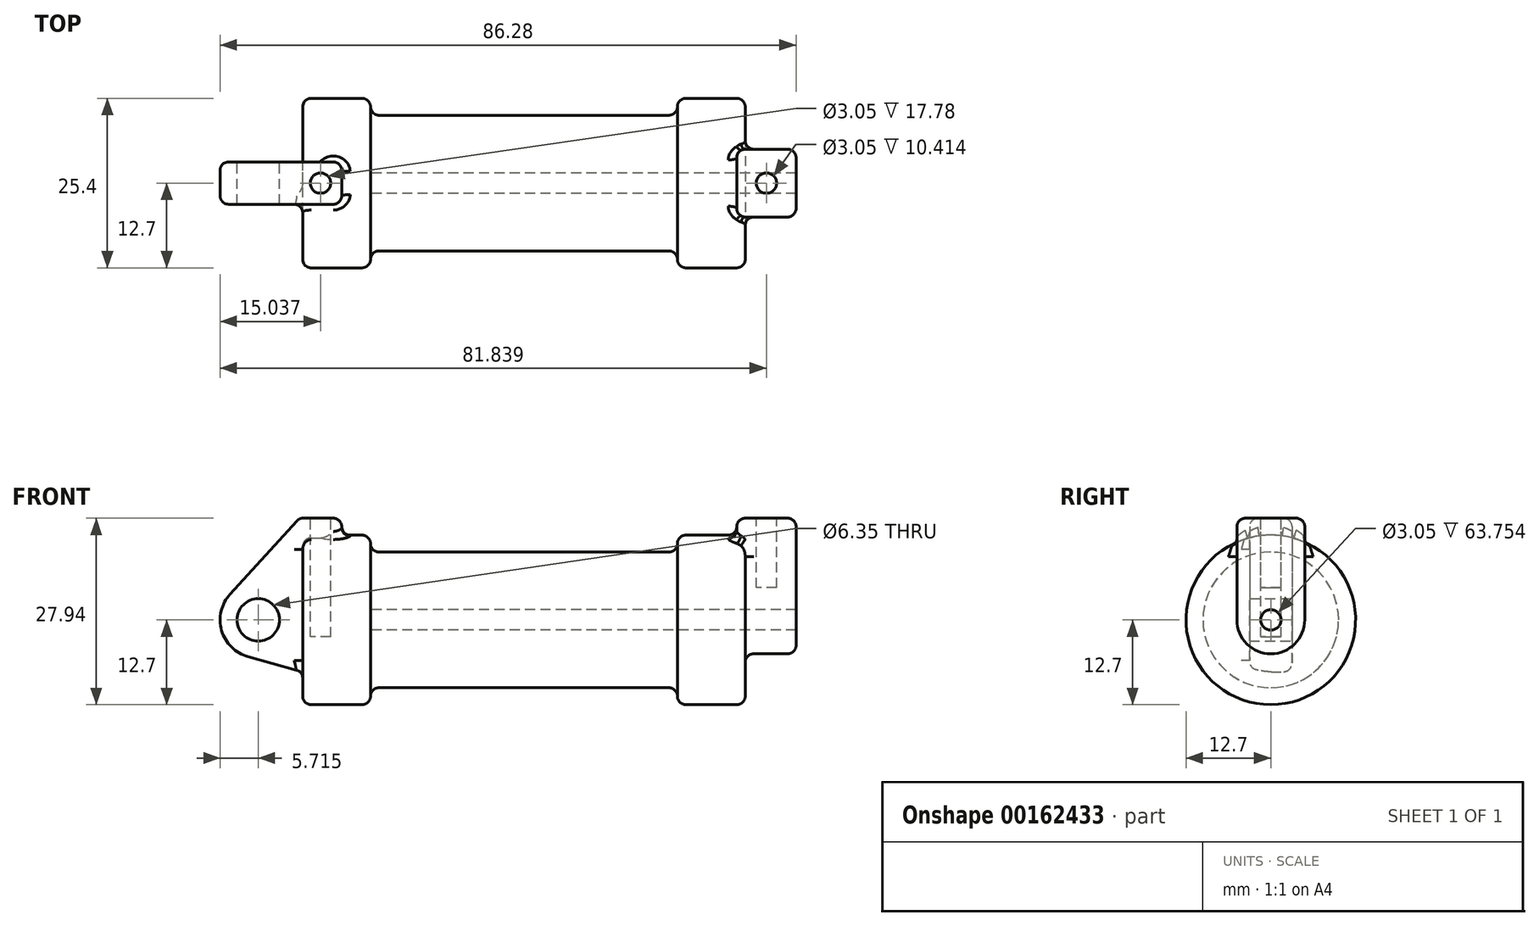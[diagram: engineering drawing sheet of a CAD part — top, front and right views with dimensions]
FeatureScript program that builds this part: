
annotation { "Feature Type Name" : "Feature", "Feature Type Description" : "" }
export const myFeature = defineFeature(function(context is Context, id is Id, definition is map)
    precondition{}
    {
        {
            var Q0;
            Q0=qCreatedBy(makeId("Front.planeOp"),FACE);
            var sketch = newSketch(context, id + "F0", { "sketchPlane" : qUnion([Q0])});
            skLineSegment(sketch, "E0", {"start": v(0, 0) * mm, "end": v(0, 12.7) * mm});
            skLineSegment(sketch, "E1", {"start": v(0, 12.7) * mm, "end": v(10.16, 12.7) * mm});
            skLineSegment(sketch, "E2", {"start": v(10.16, 12.7) * mm, "end": v(10.16, 10.16) * mm});
            skLineSegment(sketch, "E3", {"start": v(10.16, 10.16) * mm, "end": v(56.13, 10.16) * mm});
            skLineSegment(sketch, "E4", {"start": v(56.13, 10.16) * mm, "end": v(56.13, 12.7) * mm});
            skLineSegment(sketch, "E5", {"start": v(56.13, 12.7) * mm, "end": v(66.3, 12.7) * mm});
            skLineSegment(sketch, "E6", {"start": v(66.3, 12.7) * mm, "end": v(66.3, 0) * mm});
            skLineSegment(sketch, "E7", {"start": v(66.3, 0) * mm, "end": v(0, 0) * mm});
            skLineSegment(sketch, "E8", {"start": v(5.84, 15.24) * mm, "end": v(-0.5, 15.24) * mm});
            skLineSegment(sketch, "E9", {"start": v(-0.5, 15.24) * mm, "end": v(-10.88, 3.85) * mm});
            skLineSegment(sketch, "E10", {"start": v(0, 0) * mm, "end": v(-6.65, 0) * mm});
            skCircle(sketch, "E11", {"center": v(-6.65, 0) * mm, "radius": 5.72 * mm});
            skCircle(sketch, "E12", {"center": v(-6.65, 0) * mm, "radius": 3.18 * mm});
            skLineSegment(sketch, "E13", {"start": v(5.84, 15.24) * mm, "end": v(5.84, -9.4) * mm});
            skLineSegment(sketch, "E14", {"start": v(5.84, -9.4) * mm, "end": v(-8.18, -5.5) * mm});
            skSolve(sketch);
        }
        {
            var Q0;
            {var subQ0=sQuery(id+"F0.wireOp",EDGE,"E2");Q0=makeQuery(id+"F0.imprint","IMPRINT",FACE,{"disambiguationData":[TD([[makeQuery(id+"F0.imprint","IMPRINT",EDGE,{"derivedFrom":subQ0}),-1.0]])]});}
            var Q1;
            {var subQ0=sQuery(id+"F0.wireOp",EDGE,"E0");Q1=makeQuery(id+"F0.imprint","IMPRINT",FACE,{"disambiguationData":[TD([[makeQuery(id+"F0.imprint","IMPRINT",EDGE,{"derivedFrom":subQ0}),-1.0]])]});}
            var Q2;
            Q2=sQuery(id+"F0.wireOp",EDGE,"E7");
            revolve(context, id + "F1", {"entities" : qUnion([Q0, Q1]), "axis" : qUnion([Q2]), "revolveType" : RevolveType.FULL});
        }
        {
            var Q0;
            {var subQ3=sQuery(id+"F0.wireOp",EDGE,"E0");Q0=makeQuery(id+"F0.imprint","IMPRINT",FACE,{"disambiguationData":[TD([[makeQuery(id+"F0.imprint","IMPRINT",EDGE,{"derivedFrom":subQ3}),1.0]])]});}
            var Q1;
            {var subQ4=sQuery(id+"F0.wireOp",EDGE,"E12");Q1=makeQuery(id+"F0.imprint","IMPRINT",FACE,{"disambiguationData":[TD([[makeQuery(id+"F0.imprint","IMPRINT",EDGE,{"derivedFrom":subQ4}),-1.0]])]});}
            var Q2;
            {var subQ0=sQuery(id+"F0.wireOp",EDGE,"E14");Q2=makeQuery(id+"F0.imprint","IMPRINT",FACE,{"disambiguationData":[TD([[makeQuery(id+"F0.imprint","IMPRINT",EDGE,{"derivedFrom":subQ0}),-1.0]])]});}
            var Q3;
            {var subQ0=sQuery(id+"F0.wireOp",EDGE,"E0");Q3=makeQuery(id+"F0.imprint","IMPRINT",FACE,{"disambiguationData":[TD([[makeQuery(id+"F0.imprint","IMPRINT",EDGE,{"derivedFrom":subQ0}),-1.0]])]});}
            extrude(context, id + "F2", {"entities" : qUnion([Q0, Q1, Q2, Q3]), "operationType" : NewBodyOperationType.ADD, "endBound" : BoundingType.SYMMETRIC, "depth" : 6.35 * mm});
        }
        {
            var Q0;
            Q0=makeQuery(id+"F1.opRevolve","SWEPT_FACE",FACE,{"disambiguationData":[OSD([sQuery(id+"F0.wireOp",EDGE,"E6")])]});
            var sketch = newSketch(context, id + "F3", { "sketchPlane" : qUnion([Q0])});
            skCircle(sketch, "E15", {"center": v(0, 0) * mm, "radius": 5.08 * mm});
            skCircle(sketch, "E16", {"center": v(0, 0) * mm, "radius": 1.52 * mm});
            skLineSegment(sketch, "E17", {"start": v(-5.08, 0) * mm, "end": v(-5.08, 15.24) * mm});
            skLineSegment(sketch, "E18", {"start": v(-5.08, 15.24) * mm, "end": v(5.08, 15.24) * mm});
            skLineSegment(sketch, "E19", {"start": v(5.08, 15.24) * mm, "end": v(5.08, 0) * mm});
            skSolve(sketch);
        }
        {
            var Q0;
            Q0 = qSketchRegion(id + "F3", true);
            extrude(context, id + "F4", {"entities" : qUnion([Q0]), "operationType" : NewBodyOperationType.ADD, "depth" : 7.62 * mm, "hasSecondDirection" : true, "secondDirectionOppositeDirection" : true, "secondDirectionDepth" : 1.27 * mm});
        }
        {
            var Q0;
            Q0=makeQuery(id+"F4.boolean.opBoolean","SPLIT",FACE,{"disambiguationData":[TD([makeQuery(id+"F4.opExtrude","SWEPT_FACE",FACE,{"disambiguationData":[OSD([sQuery(id+"F3.wireOp",EDGE,"E16")])]})])],"derivedFrom":makeQuery(id+"F1.opRevolve","SWEPT_FACE",FACE,{"disambiguationData":[OSD([sQuery(id+"F0.wireOp",EDGE,"E6")])]})});
            var Q1;
            Q1=makeQuery(id+"F1.opRevolve","SWEPT_FACE",FACE,{"disambiguationData":[OSD([sQuery(id+"F0.wireOp",EDGE,"E2")])]});
            extrude(context, id + "F5", {"entities" : qUnion([Q0]), "operationType" : NewBodyOperationType.REMOVE, "endBound" : BoundingType.UP_TO_SURFACE, "oppositeDirection" : true, "endBoundEntityFace" : qUnion([Q1]), "depth" : 25.4 * mm});
        }
        {
            var Q0;
            Q0=makeQuery(id+"F2.opExtrude","SWEPT_FACE",FACE,{"disambiguationData":[OSD([sQuery(id+"F0.wireOp",EDGE,"E8")])]});
            var sketch = newSketch(context, id + "F6", { "sketchPlane" : qUnion([Q0])});
            skCircle(sketch, "E20", {"center": v(2.67, 0) * mm, "radius": 1.52 * mm});
            skCircle(sketch, "E21", {"center": v(69.47, 0) * mm, "radius": 1.52 * mm});
            skLineSegment(sketch, "E22.0", {"start": v(73.91, 5.08) * mm, "end": v(65.02, 5.08) * mm, "construction": true});
            skLineSegment(sketch, "E23.0", {"start": v(65.02, -5.08) * mm, "end": v(65.02, 5.08) * mm, "construction": true});
            skLineSegment(sketch, "E24.0", {"start": v(73.91, -5.08) * mm, "end": v(65.02, -5.08) * mm, "construction": true});
            skLineSegment(sketch, "E25.0", {"start": v(73.91, -5.08) * mm, "end": v(73.91, 5.08) * mm, "construction": true});
            skLineSegment(sketch, "E26.0", {"start": v(5.84, -3.18) * mm, "end": v(-0.5, -3.18) * mm, "construction": true});
            skLineSegment(sketch, "E27.0", {"start": v(-0.5, -3.18) * mm, "end": v(-0.5, 3.17) * mm, "construction": true});
            skLineSegment(sketch, "E28.0", {"start": v(5.84, 3.18) * mm, "end": v(-0.5, 3.18) * mm, "construction": true});
            skLineSegment(sketch, "E29.0", {"start": v(5.84, -3.18) * mm, "end": v(5.84, 3.17) * mm, "construction": true});
            skLineSegment(sketch, "E30", {"start": v(-0.5, 3.17) * mm, "end": v(5.84, -3.18) * mm, "construction": true});
            skLineSegment(sketch, "E31", {"start": v(-0.5, -3.18) * mm, "end": v(5.84, 3.18) * mm, "construction": true});
            skLineSegment(sketch, "E32", {"start": v(65.02, 5.08) * mm, "end": v(73.91, -5.08) * mm, "construction": true});
            skLineSegment(sketch, "E33", {"start": v(65.02, -5.08) * mm, "end": v(73.91, 5.08) * mm, "construction": true});
            skSolve(sketch);
        }
        {
            var Q0;
            Q0=makeQuery(id+"F6.imprint","IMPRINT",FACE,{"disambiguationData":[TD([[makeQuery(id+"F6.imprint","IMPRINT",EDGE,{"derivedFrom":sQuery(id+"F6.wireOp",EDGE,"E20")}),1.0]])]});
            extrude(context, id + "F7", {"entities" : qUnion([Q0]), "operationType" : NewBodyOperationType.REMOVE, "oppositeDirection" : true, "depth" : 17.78 * mm});
        }
        {
            var Q0;
            Q0=makeQuery(id+"F6.imprint","IMPRINT",FACE,{"disambiguationData":[TD([[makeQuery(id+"F6.imprint","IMPRINT",EDGE,{"derivedFrom":sQuery(id+"F6.wireOp",EDGE,"E21")}),1.0]])]});
            extrude(context, id + "F8", {"entities" : qUnion([Q0]), "operationType" : NewBodyOperationType.REMOVE, "oppositeDirection" : true, "depth" : 10.4 * mm});
        }
        {
            var Q0;
            Q0=makeQuery(id+"F1.opRevolve","SWEPT_FACE",FACE,{"disambiguationData":[OSD([sQuery(id+"F0.wireOp",EDGE,"E3")])]});
            var Q1;
            Q1=makeQuery(id+"F1.opRevolve","SWEPT_EDGE",EDGE,{"disambiguationData":[OSD([sQuery(id+"F0.wireOp",EDGE,"E1"),sQuery(id+"F0.wireOp",EDGE,"E2")])]});
            var Q2;
            Q2=makeQuery(id+"F1.opRevolve","SWEPT_EDGE",EDGE,{"disambiguationData":[OSD([sQuery(id+"F0.wireOp",EDGE,"E0"),sQuery(id+"F0.wireOp",EDGE,"E1")])]});
            var Q3;
            Q3=makeQuery(id+"F1.opRevolve","SWEPT_EDGE",EDGE,{"disambiguationData":[OSD([sQuery(id+"F0.wireOp",EDGE,"E4"),sQuery(id+"F0.wireOp",EDGE,"E5")])]});
            var Q4;
            Q4=makeQuery(id+"F1.opRevolve","SWEPT_EDGE",EDGE,{"disambiguationData":[OSD([sQuery(id+"F0.wireOp",EDGE,"E5"),sQuery(id+"F0.wireOp",EDGE,"E6")])]});
            fillet(context, id + "F9", {"entities" : qUnion([Q0, Q1, Q2, Q3, Q4]), "radius" : 1.27 * mm, "tangentPropagation" : true, "allowEdgeOverflow" : false});
        }
        {
            var Q0;
            Q0=makeQuery(id+"F2.opExtrude","CAP_EDGE",EDGE,{"disambiguationData":[OSD([sQuery(id+"F0.wireOp",EDGE,"E8")])],"isStart":false});
            var Q1;
            Q1=makeQuery(id+"F2.opExtrude","SWEPT_EDGE",EDGE,{"disambiguationData":[OSD([sQuery(id+"F0.wireOp",EDGE,"E8"),sQuery(id+"F0.wireOp",EDGE,"E13")])]});
            var Q2;
            Q2=makeQuery(id+"F2.opExtrude","CAP_EDGE",EDGE,{"disambiguationData":[OSD([sQuery(id+"F0.wireOp",EDGE,"E8")])],"isStart":true});
            var Q3;
            Q3=makeQuery(id+"F2.opExtrude","SWEPT_EDGE",EDGE,{"disambiguationData":[OSD([sQuery(id+"F0.wireOp",EDGE,"E8"),sQuery(id+"F0.wireOp",EDGE,"E9")])]});
            var Q4;
            Q4=makeQuery(id+"F2.opExtrude","SWEPT_FACE",FACE,{"disambiguationData":[OSD([sQuery(id+"F0.wireOp",EDGE,"E9")])]});
            var Q5;
            Q5=makeQuery(id+"F2.boolean.opBoolean","INTERSECT",EDGE,{"derivedFrom":[makeQuery(id+"F1.opRevolve","SWEPT_FACE",FACE,{"disambiguationData":[OSD([sQuery(id+"F0.wireOp",EDGE,"E1")])]}),makeQuery(id+"F2.opExtrude","CAP_FACE",FACE,{"disambiguationData":[OSD([sQuery(id+"F0.wireOp",EDGE,"E8"),sQuery(id+"F0.wireOp",EDGE,"E9"),sQuery(id+"F0.wireOp",EDGE,"E11"),sQuery(id+"F0.wireOp",EDGE,"E12"),sQuery(id+"F0.wireOp",EDGE,"E13"),sQuery(id+"F0.wireOp",EDGE,"E14")])],"isStart":false})]});
            var Q6;
            Q6=makeQuery(id+"F2.boolean.opBoolean","INTERSECT",EDGE,{"derivedFrom":[makeQuery(id+"F1.opRevolve","SWEPT_FACE",FACE,{"disambiguationData":[OSD([sQuery(id+"F0.wireOp",EDGE,"E1")])]}),makeQuery(id+"F2.opExtrude","SWEPT_FACE",FACE,{"disambiguationData":[OSD([sQuery(id+"F0.wireOp",EDGE,"E13")])]})]});
            var Q7;
            Q7=makeQuery(id+"F2.opExtrude","CAP_EDGE",EDGE,{"disambiguationData":[OSD([sQuery(id+"F0.wireOp",EDGE,"E13")])],"isStart":true});
            var Q8;
            Q8=makeQuery(id+"F2.opExtrude","CAP_EDGE",EDGE,{"disambiguationData":[OSD([sQuery(id+"F0.wireOp",EDGE,"E13")])],"isStart":false});
            fillet(context, id + "F10", {"entities" : qUnion([Q0, Q1, Q2, Q3, Q4, Q5, Q6, Q7, Q8]), "radius" : 1.27 * mm, "tangentPropagation" : true, "allowEdgeOverflow" : false});
        }
        {
            var Q0;
            Q0=makeQuery(id+"F4.boolean.opBoolean","INTERSECT",EDGE,{"derivedFrom":[makeQuery(id+"F1.opRevolve","SWEPT_FACE",FACE,{"disambiguationData":[OSD([sQuery(id+"F0.wireOp",EDGE,"E5")])]}),makeQuery(id+"F4.opExtrude","CAP_FACE",FACE,{"disambiguationData":[OSD([sQuery(id+"F3.wireOp",EDGE,"E15"),sQuery(id+"F3.wireOp",EDGE,"E16"),sQuery(id+"F3.wireOp",EDGE,"E17"),sQuery(id+"F3.wireOp",EDGE,"E18"),sQuery(id+"F3.wireOp",EDGE,"E19")])],"isStart":true})]});
            var Q1;
            Q1=makeQuery(id+"F4.opExtrude","CAP_EDGE",EDGE,{"disambiguationData":[OSD([sQuery(id+"F3.wireOp",EDGE,"E18")])],"isStart":true});
            var Q2;
            Q2=makeQuery(id+"F4.boolean.opBoolean","INTERSECT",EDGE,{"derivedFrom":[makeQuery(id+"F1.opRevolve","SWEPT_FACE",FACE,{"disambiguationData":[OSD([sQuery(id+"F0.wireOp",EDGE,"E6")])]}),makeQuery(id+"F4.opExtrude","SWEPT_FACE",FACE,{"disambiguationData":[OSD([sQuery(id+"F3.wireOp",EDGE,"E19")])]})]});
            var Q3;
            Q3=makeQuery(id+"F4.opExtrude","CAP_EDGE",EDGE,{"disambiguationData":[OSD([sQuery(id+"F3.wireOp",EDGE,"E17")])],"isStart":false});
            var Q4;
            Q4=makeQuery(id+"F4.opExtrude","SWEPT_EDGE",EDGE,{"disambiguationData":[OSD([sQuery(id+"F3.wireOp",EDGE,"E17"),sQuery(id+"F3.wireOp",EDGE,"E18")])]});
            var Q5;
            Q5=makeQuery(id+"F4.opExtrude","CAP_EDGE",EDGE,{"disambiguationData":[OSD([sQuery(id+"F3.wireOp",EDGE,"E18")])],"isStart":false});
            var Q6;
            Q6=makeQuery(id+"F4.opExtrude","SWEPT_EDGE",EDGE,{"disambiguationData":[OSD([sQuery(id+"F3.wireOp",EDGE,"E18"),sQuery(id+"F3.wireOp",EDGE,"E19")])]});
            var Q7;
            Q7=makeQuery(id+"F4.opExtrude","CAP_EDGE",EDGE,{"disambiguationData":[OSD([sQuery(id+"F3.wireOp",EDGE,"E17")])],"isStart":true});
            var Q8;
            Q8=makeQuery(id+"F4.opExtrude","CAP_EDGE",EDGE,{"disambiguationData":[OSD([sQuery(id+"F3.wireOp",EDGE,"E19")])],"isStart":true});
            fillet(context, id + "F11", {"entities" : qUnion([Q0, Q1, Q2, Q3, Q4, Q5, Q6, Q7, Q8]), "radius" : 1.27 * mm, "tangentPropagation" : true, "allowEdgeOverflow" : false});
        }
    });
